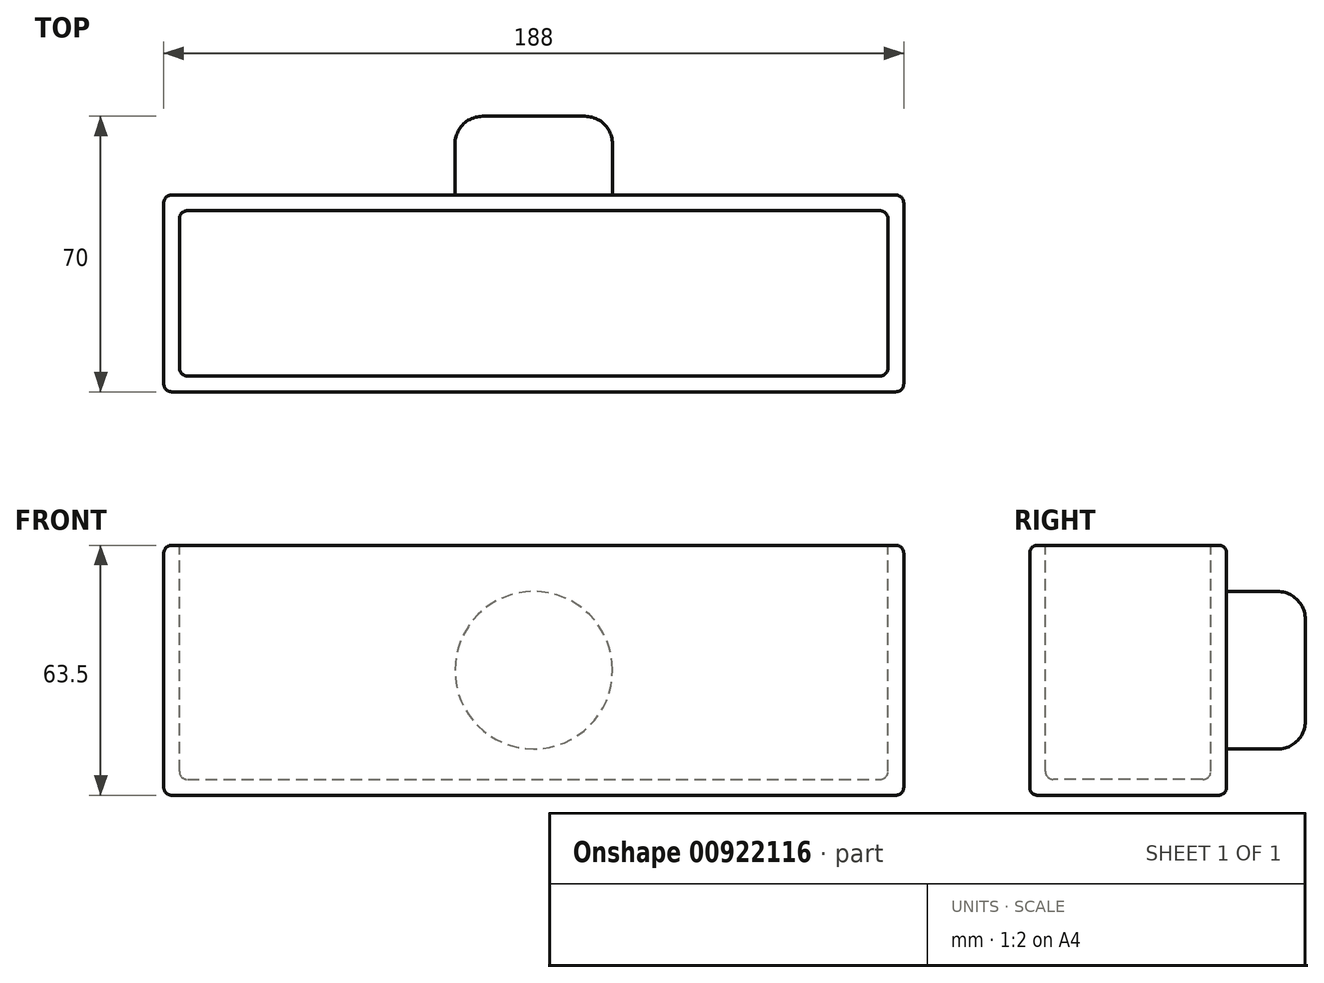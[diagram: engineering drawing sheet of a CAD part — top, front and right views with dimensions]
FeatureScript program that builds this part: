
annotation { "Feature Type Name" : "Feature", "Feature Type Description" : "" }
export const myFeature = defineFeature(function(context is Context, id is Id, definition is map)
    precondition{}
    {
        {
            var Q0;
            Q0=qCreatedBy(makeId("Front.planeOp"),FACE);
            var sketch = newSketch(context, id + "F0", { "sketchPlane" : qUnion([Q0])});
            skLineSegment(sketch, "E0", {"start": v(-62.75, 0) * mm, "end": v(125.25, 0) * mm});
            skLineSegment(sketch, "E1", {"start": v(125.25, 0) * mm, "end": v(125.25, -63.5) * mm});
            skLineSegment(sketch, "E2", {"start": v(-62.75, 0) * mm, "end": v(-62.75, -63.5) * mm});
            skLineSegment(sketch, "E3", {"start": v(125.25, -63.5) * mm, "end": v(-62.75, -63.5) * mm});
            skSolve(sketch);
        }
        {
            var Q0;
            Q0=makeQuery(id+"F0.imprint","IMPRINT",FACE,{"disambiguationData":[TD([[makeQuery(id+"F0.imprint","IMPRINT",EDGE,{"derivedFrom":sQuery(id+"F0.wireOp",EDGE,"E0")}),-1.0]])]});
            extrude(context, id + "F1", {"entities" : qUnion([Q0]), "depth" : 50 * mm, "offsetDistance" : 25 * mm});
        }
        {
            var Q0;
            Q0=qCreatedBy(makeId("Top.planeOp"),FACE);
            var sketch = newSketch(context, id + "F2", { "sketchPlane" : qUnion([Q0])});
            skLineSegment(sketch, "E4", {"start": v(-58.75, -4) * mm, "end": v(121.25, -4) * mm});
            skLineSegment(sketch, "E5", {"start": v(-58.75, -4) * mm, "end": v(-58.75, -46) * mm});
            skLineSegment(sketch, "E6", {"start": v(-58.75, -46) * mm, "end": v(121.25, -46) * mm});
            skLineSegment(sketch, "E7", {"start": v(121.25, -4) * mm, "end": v(121.25, -46) * mm});
            skSolve(sketch);
        }
        {
            var Q0;
            Q0 = qSketchRegion(id + "F2", true);
            extrude(context, id + "F3", {"entities" : qUnion([Q0]), "operationType" : NewBodyOperationType.REMOVE, "oppositeDirection" : true, "depth" : 59.5 * mm, "offsetDistance" : 25 * mm});
        }
        {
            var Q0;
            Q0=qCreatedBy(makeId("Front.planeOp"),FACE);
            var sketch = newSketch(context, id + "F4", { "sketchPlane" : qUnion([Q0])});
            skCircle(sketch, "E8", {"center": v(31.25, -31.75) * mm, "radius": 20 * mm});
            skSolve(sketch);
        }
        {
            var Q0;
            Q0 = qSketchRegion(id + "F4", true);
            extrude(context, id + "F5", {"entities" : qUnion([Q0]), "operationType" : NewBodyOperationType.ADD, "oppositeDirection" : true, "depth" : 20 * mm, "offsetDistance" : 25 * mm});
        }
        {
            var Q0;
            Q0=makeQuery(id+"F5.opExtrude","CAP_EDGE",EDGE,{"disambiguationData":[OSD([sQuery(id+"F4.wireOp",EDGE,"E8")])],"isStart":false});
            fillet(context, id + "F6", {"entities" : qUnion([Q0]), "radius" : 7 * mm, "tangentPropagation" : true, "allowEdgeOverflow" : false});
        }
        {
            var Q0;
            Q0=makeQuery(id+"F1.opExtrude","SWEPT_EDGE",EDGE,{"disambiguationData":[OSD([sQuery(id+"F0.wireOp",EDGE,"E0"),sQuery(id+"F0.wireOp",EDGE,"E1")])]});
            var Q1;
            Q1=makeQuery(id+"F1.opExtrude","SWEPT_FACE",FACE,{"disambiguationData":[OSD([sQuery(id+"F0.wireOp",EDGE,"E1")])]});
            var Q2;
            Q2=makeQuery(id+"F1.opExtrude","CAP_EDGE",EDGE,{"disambiguationData":[OSD([sQuery(id+"F0.wireOp",EDGE,"E0")])],"isStart":true});
            var Q3;
            Q3=makeQuery(id+"F1.opExtrude","CAP_EDGE",EDGE,{"disambiguationData":[OSD([sQuery(id+"F0.wireOp",EDGE,"E2")])],"isStart":false});
            var Q4;
            Q4=makeQuery(id+"F1.opExtrude","CAP_EDGE",EDGE,{"disambiguationData":[OSD([sQuery(id+"F0.wireOp",EDGE,"E0")])],"isStart":false});
            var Q5;
            Q5=makeQuery(id+"F1.opExtrude","SWEPT_EDGE",EDGE,{"disambiguationData":[OSD([sQuery(id+"F0.wireOp",EDGE,"E0"),sQuery(id+"F0.wireOp",EDGE,"E2")])]});
            var Q6;
            Q6=makeQuery(id+"F3.boolean.opBoolean","COPY",EDGE,{"derivedFrom":makeQuery(id+"F3.opExtrude","CAP_EDGE",EDGE,{"disambiguationData":[OSD([sQuery(id+"F2.wireOp",EDGE,"E6")])],"isStart":true})});
            var Q7;
            Q7=makeQuery(id+"F3.boolean.opBoolean","COPY",EDGE,{"derivedFrom":makeQuery(id+"F3.opExtrude","CAP_EDGE",EDGE,{"disambiguationData":[OSD([sQuery(id+"F2.wireOp",EDGE,"E7")])],"isStart":true})});
            var Q8;
            Q8=makeQuery(id+"F3.boolean.opBoolean","COPY",EDGE,{"derivedFrom":makeQuery(id+"F3.opExtrude","CAP_EDGE",EDGE,{"disambiguationData":[OSD([sQuery(id+"F2.wireOp",EDGE,"E6")])],"isStart":false})});
            var Q9;
            Q9=makeQuery(id+"F1.opExtrude","CAP_EDGE",EDGE,{"disambiguationData":[OSD([sQuery(id+"F0.wireOp",EDGE,"E3")])],"isStart":true});
            var Q10;
            Q10=makeQuery(id+"F3.boolean.opBoolean","COPY",EDGE,{"derivedFrom":makeQuery(id+"F3.opExtrude","SWEPT_EDGE",EDGE,{"disambiguationData":[OSD([sQuery(id+"F2.wireOp",EDGE,"E6"),sQuery(id+"F2.wireOp",EDGE,"E7")])]})});
            var Q11;
            Q11=makeQuery(id+"F3.boolean.opBoolean","COPY",EDGE,{"derivedFrom":makeQuery(id+"F3.opExtrude","CAP_EDGE",EDGE,{"disambiguationData":[OSD([sQuery(id+"F2.wireOp",EDGE,"E7")])],"isStart":false})});
            var Q12;
            Q12=makeQuery(id+"F3.boolean.opBoolean","COPY",EDGE,{"derivedFrom":makeQuery(id+"F3.opExtrude","CAP_EDGE",EDGE,{"disambiguationData":[OSD([sQuery(id+"F2.wireOp",EDGE,"E4")])],"isStart":true})});
            var Q13;
            Q13=makeQuery(id+"F3.boolean.opBoolean","COPY",EDGE,{"derivedFrom":makeQuery(id+"F3.opExtrude","CAP_EDGE",EDGE,{"disambiguationData":[OSD([sQuery(id+"F2.wireOp",EDGE,"E5")])],"isStart":true})});
            var Q14;
            Q14=makeQuery(id+"F1.opExtrude","CAP_EDGE",EDGE,{"disambiguationData":[OSD([sQuery(id+"F0.wireOp",EDGE,"E1")])],"isStart":true});
            var Q15;
            Q15=makeQuery(id+"F1.opExtrude","CAP_EDGE",EDGE,{"disambiguationData":[OSD([sQuery(id+"F0.wireOp",EDGE,"E1")])],"isStart":false});
            var Q16;
            Q16=makeQuery(id+"F3.boolean.opBoolean","COPY",EDGE,{"derivedFrom":makeQuery(id+"F3.opExtrude","SWEPT_EDGE",EDGE,{"disambiguationData":[OSD([sQuery(id+"F2.wireOp",EDGE,"E4"),sQuery(id+"F2.wireOp",EDGE,"E7")])]})});
            var Q17;
            Q17=makeQuery(id+"F3.boolean.opBoolean","COPY",EDGE,{"derivedFrom":makeQuery(id+"F3.opExtrude","CAP_EDGE",EDGE,{"disambiguationData":[OSD([sQuery(id+"F2.wireOp",EDGE,"E4")])],"isStart":false})});
            var Q18;
            Q18=makeQuery(id+"F1.opExtrude","CAP_EDGE",EDGE,{"disambiguationData":[OSD([sQuery(id+"F0.wireOp",EDGE,"E3")])],"isStart":false});
            var Q19;
            Q19=makeQuery(id+"F3.boolean.opBoolean","COPY",EDGE,{"derivedFrom":makeQuery(id+"F3.opExtrude","SWEPT_EDGE",EDGE,{"disambiguationData":[OSD([sQuery(id+"F2.wireOp",EDGE,"E5"),sQuery(id+"F2.wireOp",EDGE,"E6")])]})});
            var Q20;
            {var subQ0=sQuery(id+"F4.wireOp",EDGE,"E8");Q20=makeQuery(id+"F6.opFillet","BLEND_EDGE",EDGE,{"blendedFrom":[makeQuery(id+"F5.opExtrude","CAP_EDGE",EDGE,{"disambiguationData":[OSD([subQ0])],"isStart":false}),makeQuery(id+"F5.opExtrude","CAP_FACE",FACE,{"disambiguationData":[OSD([subQ0])],"isStart":false})],"blendedInto":[makeQuery(id+"F5.opExtrude","CAP_FACE",FACE,{"disambiguationData":[OSD([subQ0])],"isStart":false})]});}
            var Q21;
            Q21=makeQuery(id+"F1.opExtrude","SWEPT_EDGE",EDGE,{"disambiguationData":[OSD([sQuery(id+"F0.wireOp",EDGE,"E1"),sQuery(id+"F0.wireOp",EDGE,"E3")])]});
            var Q22;
            Q22=makeQuery(id+"F5.opExtrude","CAP_EDGE",EDGE,{"disambiguationData":[OSD([sQuery(id+"F4.wireOp",EDGE,"E8")])],"isStart":true});
            var Q23;
            {var subQ0=sQuery(id+"F4.wireOp",EDGE,"E8");Q23=makeQuery(id+"F6.opFillet","BLEND_EDGE",EDGE,{"blendedFrom":[makeQuery(id+"F5.opExtrude","CAP_EDGE",EDGE,{"disambiguationData":[OSD([subQ0])],"isStart":false}),makeQuery(id+"F5.opExtrude","SWEPT_FACE",FACE,{"disambiguationData":[OSD([subQ0])]})],"blendedInto":[makeQuery(id+"F5.opExtrude","SWEPT_FACE",FACE,{"disambiguationData":[OSD([subQ0])]})]});}
            var Q24;
            Q24=makeQuery(id+"F1.opExtrude","CAP_EDGE",EDGE,{"disambiguationData":[OSD([sQuery(id+"F0.wireOp",EDGE,"E2")])],"isStart":true});
            var Q25;
            Q25=makeQuery(id+"F3.boolean.opBoolean","COPY",EDGE,{"derivedFrom":makeQuery(id+"F3.opExtrude","CAP_EDGE",EDGE,{"disambiguationData":[OSD([sQuery(id+"F2.wireOp",EDGE,"E5")])],"isStart":false})});
            var Q26;
            Q26=makeQuery(id+"F3.boolean.opBoolean","COPY",EDGE,{"derivedFrom":makeQuery(id+"F3.opExtrude","SWEPT_EDGE",EDGE,{"disambiguationData":[OSD([sQuery(id+"F2.wireOp",EDGE,"E4"),sQuery(id+"F2.wireOp",EDGE,"E5")])]})});
            var Q27;
            Q27=makeQuery(id+"F1.opExtrude","SWEPT_EDGE",EDGE,{"disambiguationData":[OSD([sQuery(id+"F0.wireOp",EDGE,"E2"),sQuery(id+"F0.wireOp",EDGE,"E3")])]});
            fillet(context, id + "F7", {"entities" : qUnion([Q0, Q1, Q2, Q3, Q4, Q5, Q6, Q7, Q8, Q9, Q10, Q11, Q12, Q13, Q14, Q15, Q16, Q17, Q18, Q19, Q20, Q21, Q22, Q23, Q24, Q25, Q26, Q27]), "radius" : 2 * mm, "tangentPropagation" : true, "allowEdgeOverflow" : false});
        }
    });
